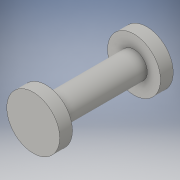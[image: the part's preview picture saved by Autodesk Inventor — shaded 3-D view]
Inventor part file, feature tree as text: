
AUTODESK INVENTOR PART (.ipt)
format: ipt  version: 2016 (Build 200138000, 138)  size: 105,472 bytes
history: native  units: in
note: dims shown in document units (in); Inventor stores cm internally (conversion verified against a paired STEP export)
features: extrude x3, sketch x3
ambient origin geometry x8: Origin, YZ Plane, XZ Plane, XY Plane, X Axis, Y Axis, Z Axis, Center Point
bodies: Solid1 (feature_tree)
feature tree (6):
  extrude  "Extrusion1"  Depth=0.416in TaperAngle=0.0deg
  extrude  "Extrusion2"  Depth=0.06in TaperAngle=0.0deg
  extrude  "Extrusion3"  [1 undecoded]
  sketch  "Sketch1"  dims[d0=0.125in d1=0.416in d2=0.0in]
  sketch  "Sketch2"  dims[d3=0.25in d4=0.06in d5=0.0in]
  sketch  "Sketch3"  dims[d6=0.06in d7=0.0in]
note: 1 required parameter value undecoded (feature->parameter linkage not recoverable at this tier; creation-order binding heuristic only, values carry confidence <= 0.55)
